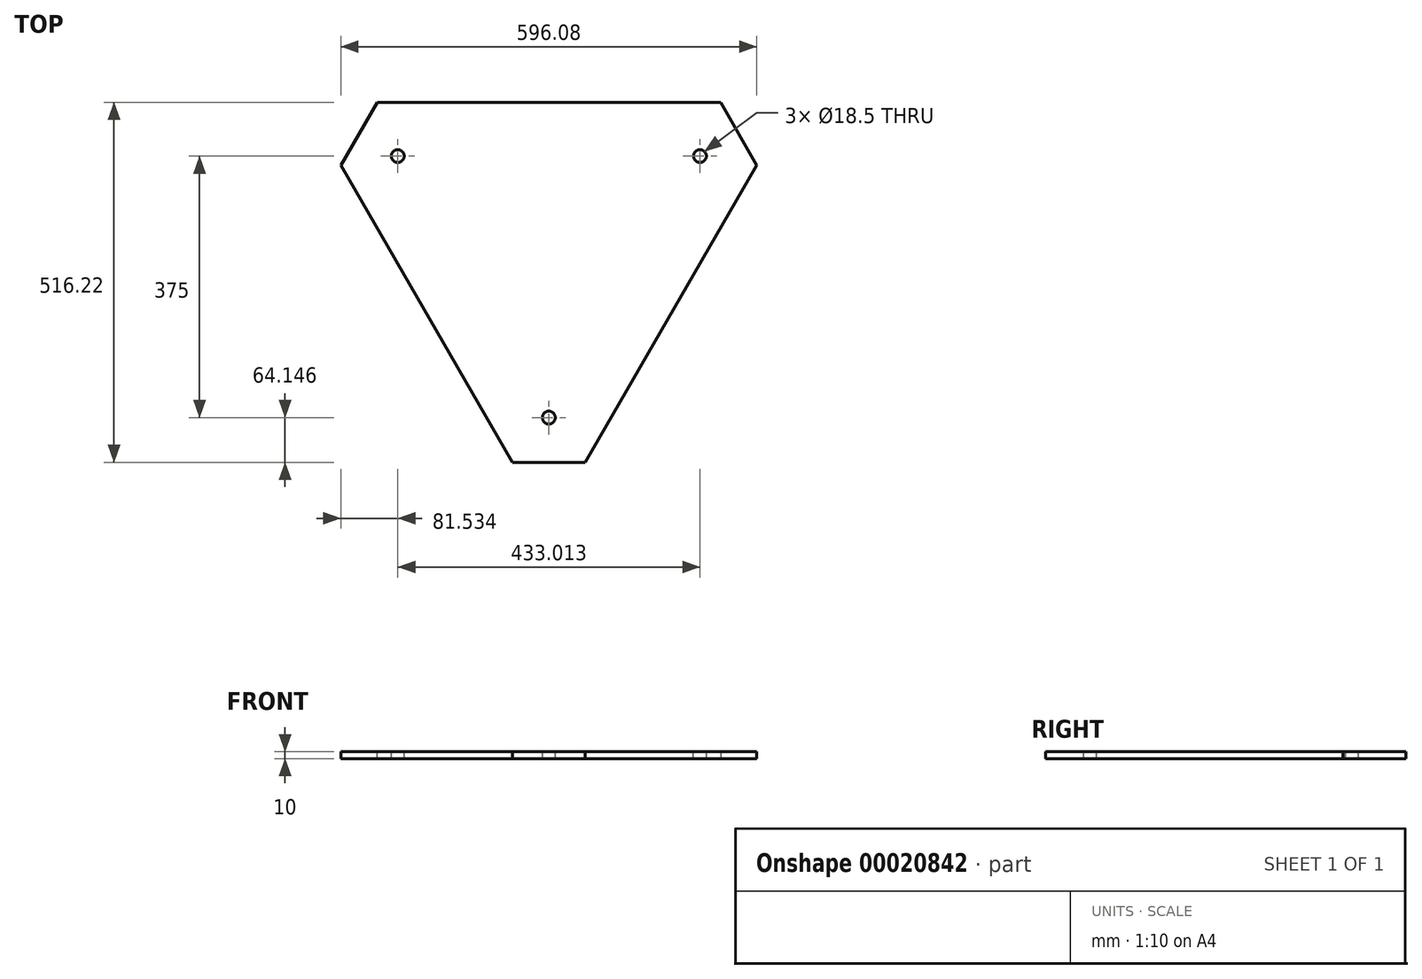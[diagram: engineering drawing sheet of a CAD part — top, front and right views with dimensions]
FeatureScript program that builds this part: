
annotation { "Feature Type Name" : "Feature", "Feature Type Description" : "" }
export const myFeature = defineFeature(function(context is Context, id is Id, definition is map)
    precondition{}
    {
        {
            var Q0;
            Q0=qCreatedBy(makeId("Top.planeOp"),FACE);
            var sketch = newSketch(context, id + "F0", { "sketchPlane" : qUnion([Q0])});
            skLineSegment(sketch, "E0", {"start": v(0, 303.1) * mm, "end": v(0, -303.1) * mm, "construction": true});
            skLineSegment(sketch, "E1", {"start": v(0, -303.1) * mm, "end": v(350, 303.1) * mm});
            skLineSegment(sketch, "E2", {"start": v(350, 303.1) * mm, "end": v(0, 303.1) * mm});
            skPoint(sketch, "E3", {"position": v(175, 0) * mm});
            skLineSegment(sketch, "E4", {"start": v(175, 0) * mm, "end": v(0, 101.04) * mm, "construction": true});
            skLineSegment(sketch, "E5.MirrorCS", {"start": v(-350, 303.1) * mm, "end": v(0, 303.1) * mm});
            skLineSegment(sketch, "E6.MirrorCS", {"start": v(0, -303.1) * mm, "end": v(-350, 303.1) * mm});
            skPoint(sketch, "E7", {"position": v(0, -148.96) * mm});
            skPoint(sketch, "E8.1.0", {"position": v(216.5, 226.04) * mm});
            skPoint(sketch, "E8.2.0", {"position": v(-216.5, 226.04) * mm});
            skPoint(sketch, "E8.center", {"position": v(0, 101.04) * mm});
            skSolve(sketch);
        }
        {
            var Q0;
            Q0 = qSketchRegion(id + "F0", true);
            extrude(context, id + "F1", {"entities" : qUnion([Q0]), "oppositeDirection" : true, "depth" : 10 * mm});
        }
        {
            var Q0;
            Q0=sQuery(id+"F0.wireOp",VERTEX,"E8.2.0");
            var Q1;
            Q1=sQuery(id+"F0.wireOp",VERTEX,"E8.1.0");
            var Q2;
            Q2=sQuery(id+"F0.wireOp",VERTEX,"E7");
            var Q3;
            Q3=makeQuery(id+"F1.opExtrude","SWEPT_BODY",BODY,{"disambiguationData":[OSD([sQuery(id+"F0.wireOp",EDGE,"E1"),sQuery(id+"F0.wireOp",EDGE,"E2"),sQuery(id+"F0.wireOp",EDGE,"E5.MirrorCS"),sQuery(id+"F0.wireOp",EDGE,"E6.MirrorCS")])]});
            hole(context, id + "F2", {"style" : HoleStyle.SIMPLE, "holeDiameter" : 18.5 * mm, "endStyle" : HoleEndStyle.THROUGH, "locations" : qUnion([Q0, Q1, Q2]), "scope" : qUnion([Q3])});
        }
        {
            var Q0;
            Q0=makeQuery(id+"F1.opExtrude","SWEPT_EDGE",EDGE,{"disambiguationData":[OSD([sQuery(id+"F0.wireOp",EDGE,"E5.MirrorCS"),sQuery(id+"F0.wireOp",EDGE,"E6.MirrorCS")])]});
            var Q1;
            Q1=makeQuery(id+"F1.opExtrude","SWEPT_EDGE",EDGE,{"disambiguationData":[OSD([sQuery(id+"F0.wireOp",EDGE,"E1"),sQuery(id+"F0.wireOp",EDGE,"E2")])]});
            var Q2;
            Q2=makeQuery(id+"F1.opExtrude","SWEPT_EDGE",EDGE,{"disambiguationData":[OSD([sQuery(id+"F0.wireOp",EDGE,"E1"),sQuery(id+"F0.wireOp",EDGE,"E6.MirrorCS")])]});
            chamfer(context, id + "F3", {"entities" : qUnion([Q0, Q1, Q2]), "width" : 60 * mm, "tangentPropagation" : true});
        }
    });
